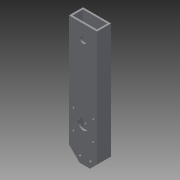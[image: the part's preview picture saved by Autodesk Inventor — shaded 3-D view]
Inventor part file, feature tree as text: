
AUTODESK INVENTOR PART (.ipt)
format: ipt  version: 2013 (Build 170138000, 138)  size: 166,912 bytes
history: native  units: in
note: dims shown in document units (in); Inventor stores cm internally (conversion verified against a paired STEP export)
features: extrude x6, sketch x6
ambient origin geometry x8: Origin, YZ Plane, XZ Plane, XY Plane, X Axis, Y Axis, Z Axis, Center Point
bodies: Solid1 (feature_tree)
feature tree (12):
  extrude  "Extrusion1"  Depth=1.0in
  extrude  "Extrusion2"  Depth=0.75in
  extrude  "Extrusion3"  Depth=1.0in
  extrude  "Extrusion4"  Depth=7.0in
  extrude  "Extrusion5"  Depth=0.25in
  extrude  "Extrusion6"  Depth=0.5in
  sketch  "Sketch1"  dims[d0=2.0in d1=1.0in]
  sketch  "Sketch2"  dims[d2=1.75in d3=0.75in]
  sketch  "Sketch3"  dims[d4=9.0in d5=0.0in d6=1.0in]
  sketch  "Sketch4"  dims[d7=0.5in d8=7.0in]
  sketch  "Sketch5"  dims[d9=90.0deg d10=0.25in]
  sketch  "Sketch6"  dims[d11=90.0deg d12=0.5in d13=0.75in d14=0.0in d15=0.2in d16=0.2in d17=9.0in d18=0.0in d19=0.25in d20=0.0in d21=25.0in d22=0.0in d23=25.0in d24=0.0in d25=2.5in d26=90.0deg d27=0.75in d28=1.0in d29=45.0deg d30=2.0in d31=0.16in d32=0.16in d33=0.16in d34=0.16in d35=25.0in d36=0.0in]
